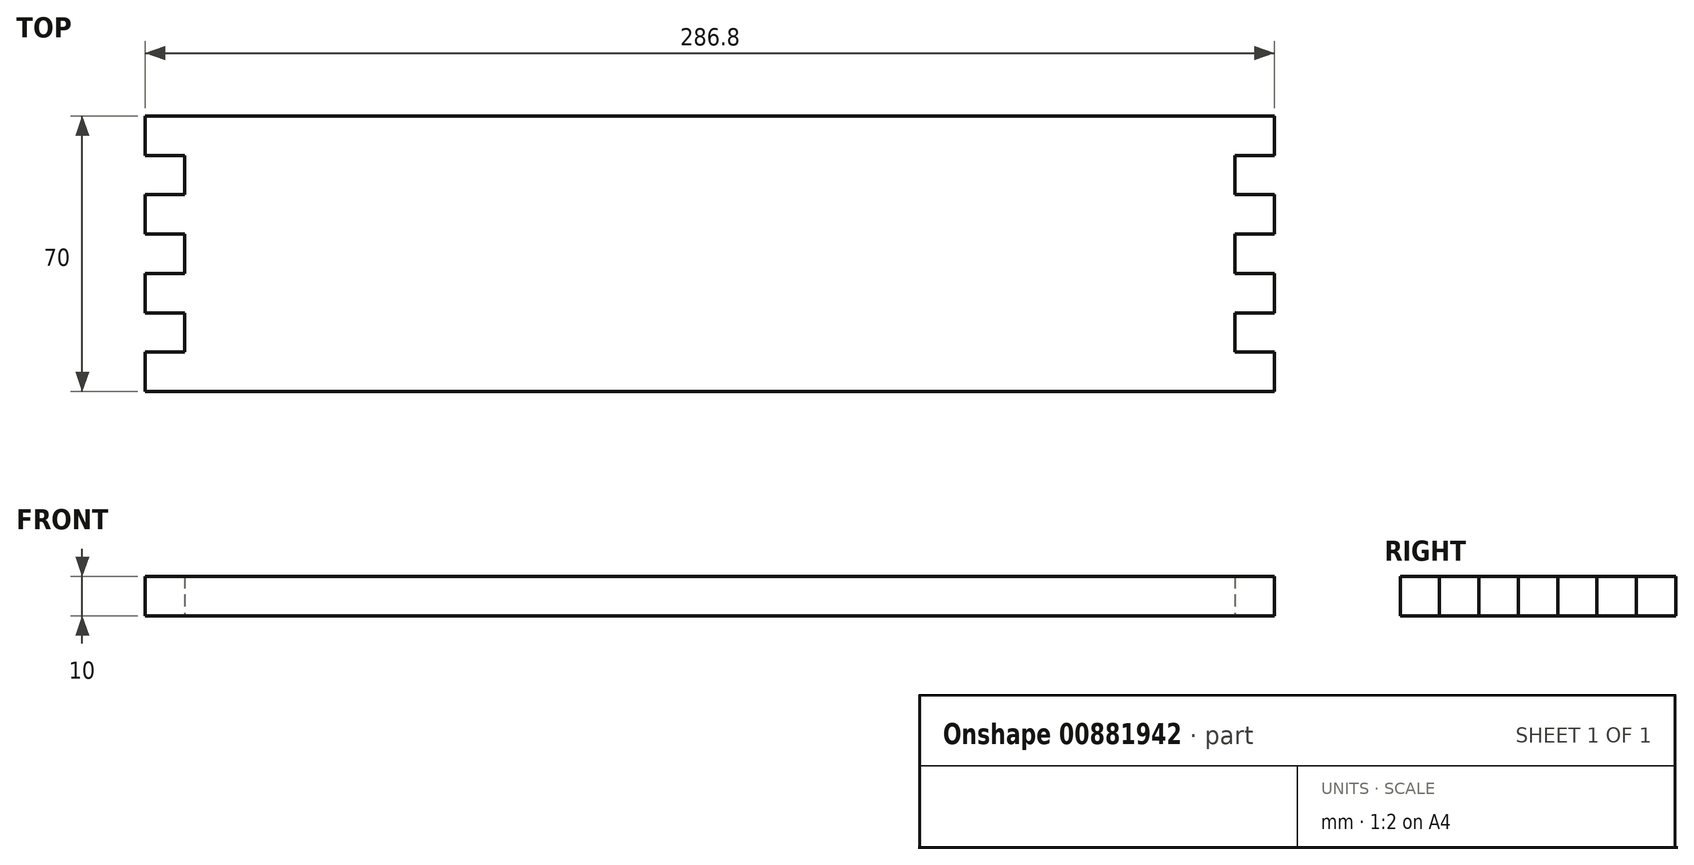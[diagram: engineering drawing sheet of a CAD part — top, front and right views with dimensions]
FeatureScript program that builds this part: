
annotation { "Feature Type Name" : "Feature", "Feature Type Description" : "" }
export const myFeature = defineFeature(function(context is Context, id is Id, definition is map)
    precondition{}
    {
        {
            var Q0;
            Q0=qCreatedBy(makeId("Top.planeOp"),FACE);
            var sketch = newSketch(context, id + "F0", { "sketchPlane" : qUnion([Q0])});
            skLineSegment(sketch, "E0.bottom", {"start": v(-145.63, 36.94) * mm, "end": v(141.17, 36.94) * mm});
            skLineSegment(sketch, "E0.top", {"start": v(-145.63, -33.06) * mm, "end": v(141.17, -33.06) * mm});
            skLineSegment(sketch, "E0.left", {"start": v(-145.63, 36.94) * mm, "end": v(-145.63, -33.06) * mm});
            skLineSegment(sketch, "E0.right", {"start": v(141.17, 36.94) * mm, "end": v(141.17, -33.06) * mm});
            skLineSegment(sketch, "E1.bottom", {"start": v(-145.63, 36.94) * mm, "end": v(-135.63, 36.94) * mm});
            skLineSegment(sketch, "E1.top", {"start": v(-145.63, -33.06) * mm, "end": v(-135.63, -33.06) * mm});
            skLineSegment(sketch, "E1.right", {"start": v(-135.63, 36.94) * mm, "end": v(-135.63, -33.06) * mm});
            skLineSegment(sketch, "E2.bottom", {"start": v(141.17, 36.94) * mm, "end": v(131.17, 36.94) * mm});
            skLineSegment(sketch, "E2.top", {"start": v(141.17, -33.06) * mm, "end": v(131.17, -33.06) * mm});
            skLineSegment(sketch, "E2.right", {"start": v(131.17, 36.94) * mm, "end": v(131.17, -33.06) * mm});
            skLineSegment(sketch, "E3.left", {"start": v(-145.63, 36.94) * mm, "end": v(-145.63, 26.94) * mm});
            skLineSegment(sketch, "E4.bottom", {"start": v(131.17, 36.94) * mm, "end": v(141.17, 36.94) * mm});
            skLineSegment(sketch, "E4.top", {"start": v(131.17, 26.94) * mm, "end": v(141.17, 26.94) * mm});
            skLineSegment(sketch, "E4.left", {"start": v(131.17, 36.94) * mm, "end": v(131.17, 26.94) * mm});
            skLineSegment(sketch, "E4.right", {"start": v(141.17, 36.94) * mm, "end": v(141.17, 26.94) * mm});
            skLineSegment(sketch, "E5.MirrorCS", {"start": v(141.17, 16.94) * mm, "end": v(131.17, 16.94) * mm});
            skLineSegment(sketch, "E6.MirrorCS", {"start": v(131.17, 6.94) * mm, "end": v(141.17, 6.94) * mm});
            skLineSegment(sketch, "E7.MirrorCS", {"start": v(141.17, -3.06) * mm, "end": v(131.17, -3.06) * mm});
            skLineSegment(sketch, "E8.MirrorCS", {"start": v(131.17, -13.06) * mm, "end": v(141.17, -13.06) * mm});
            skLineSegment(sketch, "E9.MirrorCS", {"start": v(141.17, -23.06) * mm, "end": v(131.17, -23.06) * mm});
            skLineSegment(sketch, "E10.MirrorCS", {"start": v(131.17, -33.06) * mm, "end": v(141.17, -33.06) * mm});
            skLineSegment(sketch, "E11.top", {"start": v(-145.63, 26.94) * mm, "end": v(-135.63, 26.94) * mm});
            skLineSegment(sketch, "E11.right", {"start": v(-135.63, 36.94) * mm, "end": v(-135.63, 26.94) * mm});
            skLineSegment(sketch, "E12.MirrorCS", {"start": v(-145.63, 16.94) * mm, "end": v(-135.63, 16.94) * mm});
            skLineSegment(sketch, "E13.MirrorCS", {"start": v(-145.63, 6.94) * mm, "end": v(-135.63, 6.94) * mm});
            skLineSegment(sketch, "E14.MirrorCS", {"start": v(-145.63, -3.06) * mm, "end": v(-135.63, -3.06) * mm});
            skLineSegment(sketch, "E15.MirrorCS", {"start": v(-145.63, -13.06) * mm, "end": v(-135.63, -13.06) * mm});
            skLineSegment(sketch, "E16.MirrorCS", {"start": v(-145.63, -23.06) * mm, "end": v(-135.63, -23.06) * mm});
            skSolve(sketch);
        }
        {
            var Q0;
            {var subQ0=sQuery(id+"F0.wireOp",EDGE,"E1.right");var subQ1=sQuery(id+"F0.wireOp",EDGE,"E0.bottom");var subQ2=makeQuery(id+"F0.imprint","INTERSECT",VERTEX,{"derivedFrom":[subQ1,subQ0]});Q0=makeQuery(id+"F0.imprint","IMPRINT",FACE,{"disambiguationData":[TD([[makeQuery(id+"F0.imprint","IMPRINT",EDGE,{"disambiguationData":[TD([[subQ2,-1.0]])],"derivedFrom":subQ1}),-1.0]])]});}
            var Q1;
            {var subQ5=sQuery(id+"F0.wireOp",EDGE,"E11.top");Q1=makeQuery(id+"F0.imprint","IMPRINT",FACE,{"disambiguationData":[TD([[makeQuery(id+"F0.imprint","IMPRINT",EDGE,{"derivedFrom":subQ5}),1.0]])]});}
            var Q2;
            {var subQ0=sQuery(id+"F0.wireOp",EDGE,"E12.MirrorCS");Q2=makeQuery(id+"F0.imprint","IMPRINT",FACE,{"disambiguationData":[TD([[makeQuery(id+"F0.imprint","IMPRINT",EDGE,{"derivedFrom":subQ0}),-1.0]])]});}
            var Q3;
            {var subQ0=sQuery(id+"F0.wireOp",EDGE,"E14.MirrorCS");Q3=makeQuery(id+"F0.imprint","IMPRINT",FACE,{"disambiguationData":[TD([[makeQuery(id+"F0.imprint","IMPRINT",EDGE,{"derivedFrom":subQ0}),-1.0]])]});}
            var Q4;
            {var subQ2=sQuery(id+"F0.wireOp",EDGE,"E16.MirrorCS");Q4=makeQuery(id+"F0.imprint","IMPRINT",FACE,{"disambiguationData":[TD([[makeQuery(id+"F0.imprint","IMPRINT",EDGE,{"derivedFrom":subQ2}),-1.0]])]});}
            var Q5;
            {var subQ5=sQuery(id+"F0.wireOp",EDGE,"f68d17bd-8033-4fb8-93ba-191072b4510d0.MirrorCS");Q5=makeQuery(id+"F0.imprint","IMPRINT",FACE,{"disambiguationData":[TD([[makeQuery(id+"F0.imprint","IMPRINT",EDGE,{"derivedFrom":subQ5}),-1.0]])]});}
            var Q6;
            {var subQ5=sQuery(id+"F0.wireOp",EDGE,"E4.top");Q6=makeQuery(id+"F0.imprint","IMPRINT",FACE,{"disambiguationData":[TD([[makeQuery(id+"F0.imprint","IMPRINT",EDGE,{"derivedFrom":subQ5}),1.0]])]});}
            var Q7;
            {var subQ0=sQuery(id+"F0.wireOp",EDGE,"E5.MirrorCS");Q7=makeQuery(id+"F0.imprint","IMPRINT",FACE,{"disambiguationData":[TD([[makeQuery(id+"F0.imprint","IMPRINT",EDGE,{"derivedFrom":subQ0}),1.0]])]});}
            var Q8;
            {var subQ0=sQuery(id+"F0.wireOp",EDGE,"E7.MirrorCS");Q8=makeQuery(id+"F0.imprint","IMPRINT",FACE,{"disambiguationData":[TD([[makeQuery(id+"F0.imprint","IMPRINT",EDGE,{"derivedFrom":subQ0}),1.0]])]});}
            var Q9;
            {var subQ0=sQuery(id+"F0.wireOp",EDGE,"E9.MirrorCS");Q9=makeQuery(id+"F0.imprint","IMPRINT",FACE,{"disambiguationData":[TD([[makeQuery(id+"F0.imprint","IMPRINT",EDGE,{"derivedFrom":subQ0}),1.0]])]});}
            var Q10;
            {var subQ5=sQuery(id+"F0.wireOp",EDGE,"e518cc57-b2af-43e8-af13-6bb7c84993f30.MirrorCS");Q10=makeQuery(id+"F0.imprint","IMPRINT",FACE,{"disambiguationData":[TD([[makeQuery(id+"F0.imprint","IMPRINT",EDGE,{"derivedFrom":subQ5}),1.0]])]});}
            extrude(context, id + "F1", {"entities" : qUnion([Q0, Q1, Q2, Q3, Q4, Q5, Q6, Q7, Q8, Q9, Q10]), "depth" : 10 * mm, "offsetDistance" : 25 * mm});
        }
    });
